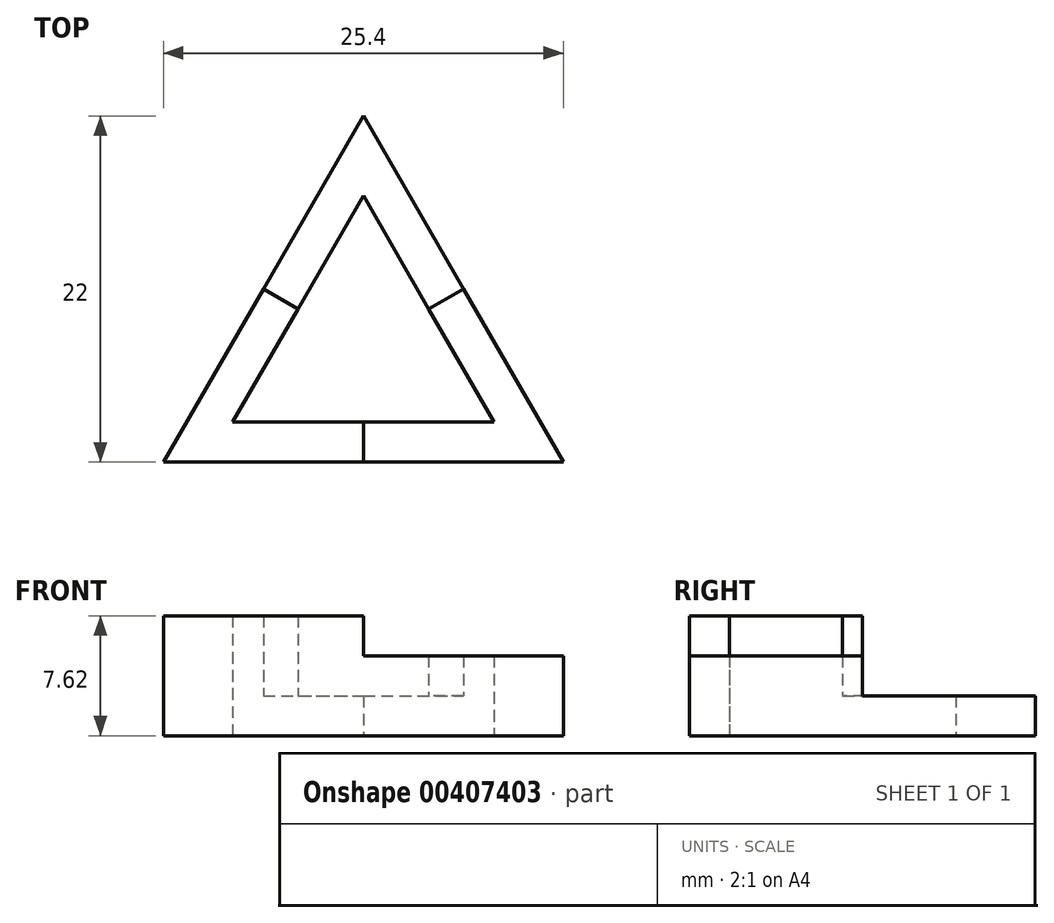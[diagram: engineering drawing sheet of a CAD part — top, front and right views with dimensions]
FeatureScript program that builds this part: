
annotation { "Feature Type Name" : "Feature", "Feature Type Description" : "" }
export const myFeature = defineFeature(function(context is Context, id is Id, definition is map)
    precondition{}
    {
        {
            var Q0;
            Q0=qCreatedBy(makeId("Top.planeOp"),FACE);
            var sketch = newSketch(context, id + "F0", { "sketchPlane" : qUnion([Q0])});
            skLineSegment(sketch, "E0", {"start": v(-37.13, -14.95) * mm, "end": v(-11.73, -14.95) * mm});
            skLineSegment(sketch, "E1", {"start": v(-37.13, -14.95) * mm, "end": v(-24.43, 7.05) * mm});
            skPoint(sketch, "E1.endSnap0", {"position": v(-24.43, -14.95) * mm});
            skLineSegment(sketch, "E2", {"start": v(-24.43, 7.05) * mm, "end": v(-11.73, -14.95) * mm});
            skLineSegment(sketch, "E3", {"start": v(-24.43, -14.95) * mm, "end": v(-24.43, -12.4) * mm});
            skLineSegment(sketch, "E4", {"start": v(-18.08, -3.95) * mm, "end": v(-20.28, -5.22) * mm});
            skLineSegment(sketch, "E5", {"start": v(-30.78, -3.95) * mm, "end": v(-28.58, -5.22) * mm});
            skLineSegment(sketch, "E6", {"start": v(-28.58, -5.22) * mm, "end": v(-24.43, 1.97) * mm});
            skLineSegment(sketch, "E7", {"start": v(-24.43, 1.97) * mm, "end": v(-20.28, -5.22) * mm});
            skLineSegment(sketch, "E8", {"start": v(-20.28, -5.22) * mm, "end": v(-16.13, -12.4) * mm});
            skLineSegment(sketch, "E9", {"start": v(-16.13, -12.4) * mm, "end": v(-24.43, -12.4) * mm});
            skLineSegment(sketch, "E10", {"start": v(-28.58, -5.22) * mm, "end": v(-32.73, -12.4) * mm});
            skLineSegment(sketch, "E11", {"start": v(-32.73, -12.4) * mm, "end": v(-24.43, -12.4) * mm});
            skSolve(sketch);
        }
        {
            var Q0;
            {var subQ0=sQuery(id+"F0.wireOp",EDGE,"E4");Q0=makeQuery(id+"F0.imprint","IMPRINT",FACE,{"disambiguationData":[TD([[makeQuery(id+"F0.imprint","IMPRINT",EDGE,{"derivedFrom":subQ0}),-1.0]])]});}
            extrude(context, id + "F1", {"entities" : qUnion([Q0]), "depth" : 2.54 * mm});
        }
        {
            var Q0;
            {var subQ4=sQuery(id+"F0.wireOp",EDGE,"E3");Q0=makeQuery(id+"F0.imprint","IMPRINT",FACE,{"disambiguationData":[TD([[makeQuery(id+"F0.imprint","IMPRINT",EDGE,{"derivedFrom":subQ4}),-1.0]])]});}
            extrude(context, id + "F2", {"entities" : qUnion([Q0]), "operationType" : NewBodyOperationType.ADD, "depth" : 5.08 * mm});
        }
        {
            var Q0;
            {var subQ1=sQuery(id+"F0.wireOp",EDGE,"E3");Q0=makeQuery(id+"F0.imprint","IMPRINT",FACE,{"disambiguationData":[TD([[makeQuery(id+"F0.imprint","IMPRINT",EDGE,{"derivedFrom":subQ1}),1.0]])]});}
            extrude(context, id + "F3", {"entities" : qUnion([Q0]), "operationType" : NewBodyOperationType.ADD, "depth" : 7.62 * mm});
        }
    });
